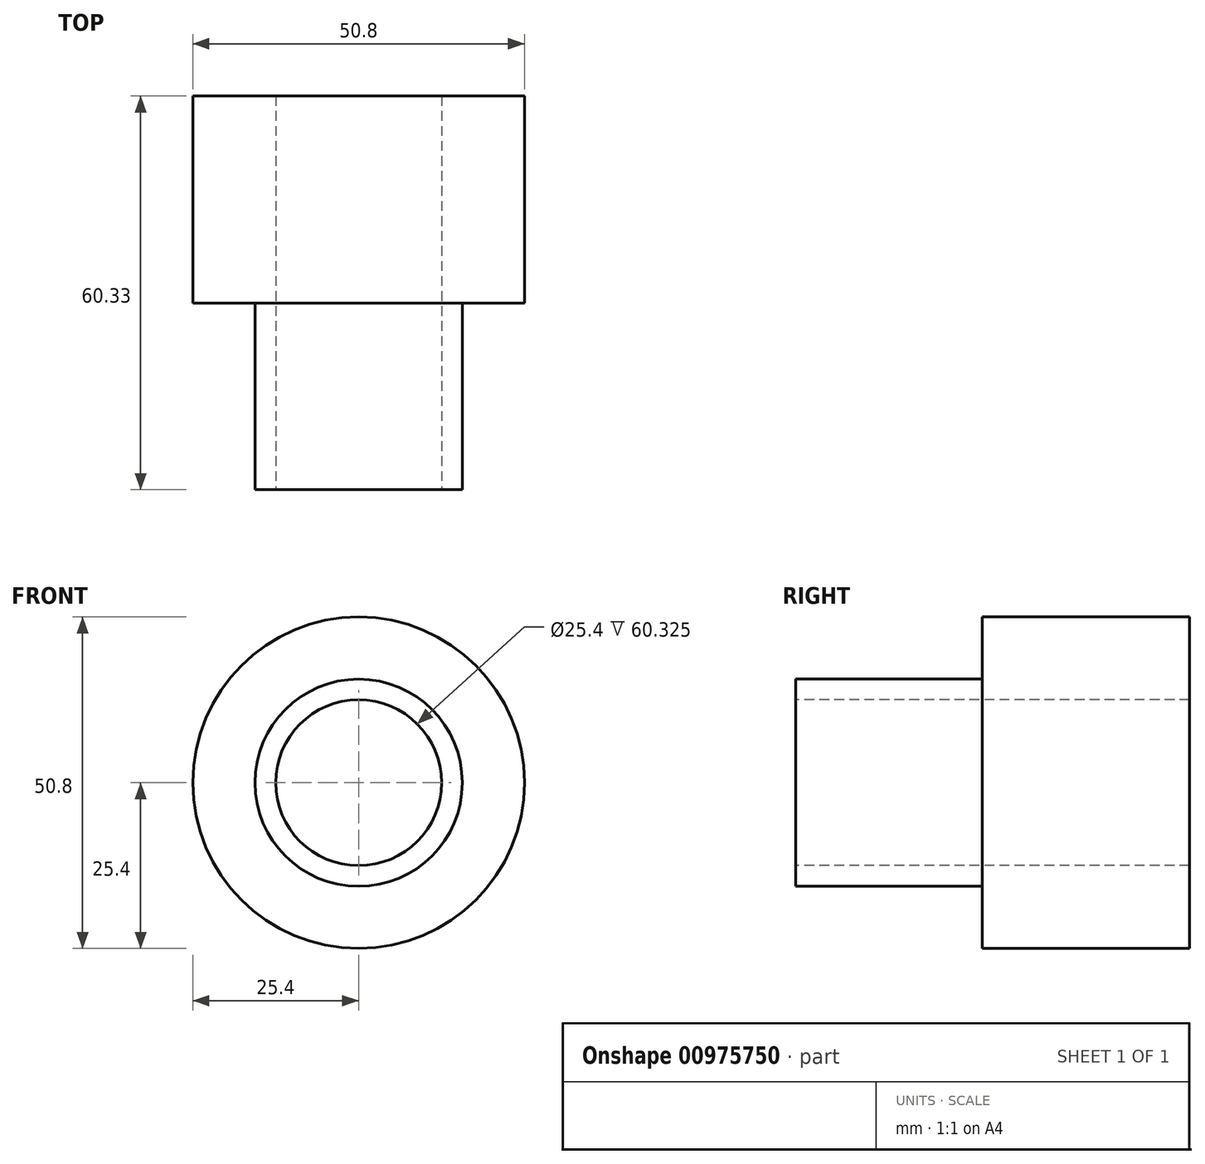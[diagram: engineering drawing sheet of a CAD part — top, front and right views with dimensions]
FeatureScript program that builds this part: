
annotation { "Feature Type Name" : "Feature", "Feature Type Description" : "" }
export const myFeature = defineFeature(function(context is Context, id is Id, definition is map)
    precondition{}
    {
        {
            var Q0;
            Q0=qCreatedBy(makeId("Front.planeOp"),FACE);
            var sketch = newSketch(context, id + "F0", { "sketchPlane" : qUnion([Q0])});
            skCircle(sketch, "E0", {"center": v(0, 0) * mm, "radius": 25.4 * mm});
            skSolve(sketch);
        }
        {
            var Q0;
            Q0=makeQuery(id+"F0.imprint","IMPRINT",FACE,{"disambiguationData":[TD([[makeQuery(id+"F0.imprint","IMPRINT",EDGE,{"derivedFrom":sQuery(id+"F0.wireOp",EDGE,"E0")}),1.0]])]});
            var Q1;
            Q1=sQuery(id+"F0.wireOp",EDGE,"E0");
            extrude(context, id + "F1", {"entities" : qUnion([Q0]), "flatOperationType" : FlatOperationType.REMOVE, "surfaceEntities" : qUnion([Q1]), "oppositeDirection" : true, "depth" : 31.75 * mm, "offsetDistance" : 25.4 * mm, "domain" : OperationDomain.MODEL});
        }
        {
            var Q0;
            Q0=makeQuery(id+"F1.opExtrude","CAP_FACE",FACE,{"disambiguationData":[OSD([sQuery(id+"F0.wireOp",EDGE,"E0")])],"isStart":true});
            var sketch = newSketch(context, id + "F2", { "sketchPlane" : qUnion([Q0])});
            skCircle(sketch, "E1", {"center": v(0, 0) * mm, "radius": 15.88 * mm});
            skSolve(sketch);
        }
        {
            var Q0;
            Q0 = qSketchRegion(id + "F2", true);
            extrude(context, id + "F3", {"entities" : qUnion([Q0]), "operationType" : NewBodyOperationType.ADD, "depth" : 28.57 * mm, "offsetDistance" : 25.4 * mm});
        }
        {
            var Q0;
            Q0=makeQuery(id+"F3.opExtrude","CAP_FACE",FACE,{"disambiguationData":[OSD([sQuery(id+"F2.wireOp",EDGE,"E1")])],"isStart":false});
            var sketch = newSketch(context, id + "F4", { "sketchPlane" : qUnion([Q0])});
            skCircle(sketch, "E2", {"center": v(0, 0) * mm, "radius": 12.7 * mm});
            skSolve(sketch);
        }
        {
            var Q0;
            Q0=makeQuery(id+"F4.imprint","IMPRINT",FACE,{"disambiguationData":[TD([[makeQuery(id+"F4.imprint","IMPRINT",EDGE,{"derivedFrom":sQuery(id+"F4.wireOp",EDGE,"E2")}),1.0]])]});
            extrude(context, id + "F5", {"entities" : qUnion([Q0]), "operationType" : NewBodyOperationType.REMOVE, "oppositeDirection" : true, "depth" : 60.32 * mm, "offsetDistance" : 25.4 * mm});
        }
    });
